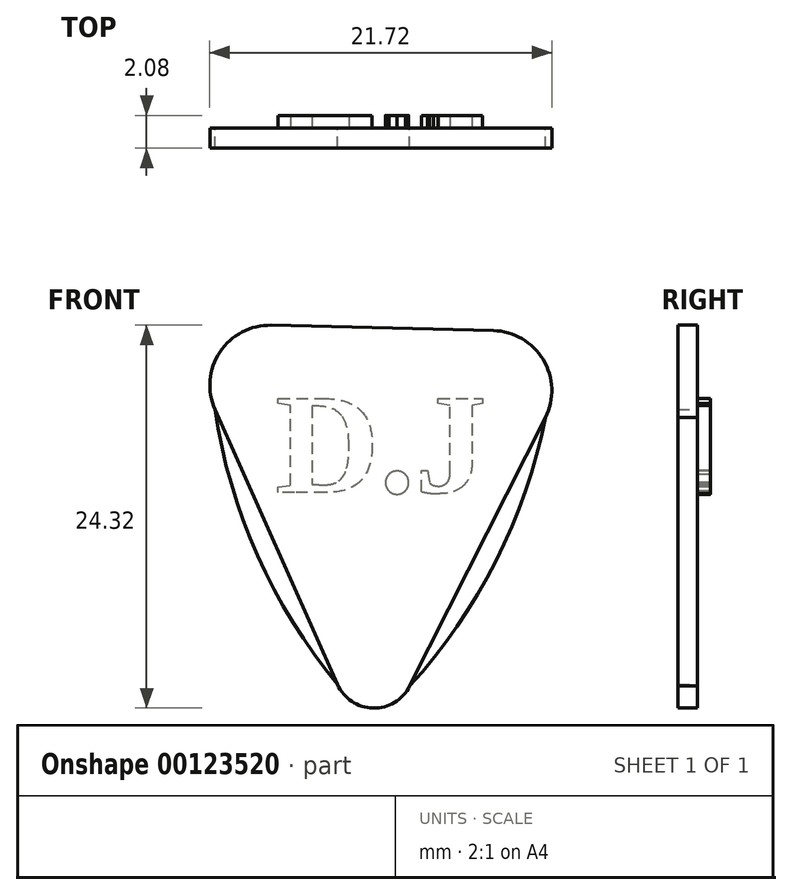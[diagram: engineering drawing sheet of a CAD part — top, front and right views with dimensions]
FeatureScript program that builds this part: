
annotation { "Feature Type Name" : "Feature", "Feature Type Description" : "" }
export const myFeature = defineFeature(function(context is Context, id is Id, definition is map)
    precondition{}
    {
        {
            var Q0;
            Q0=qCreatedBy(makeId("Front.planeOp"),FACE);
            var sketch = newSketch(context, id + "F0", { "sketchPlane" : qUnion([Q0])});
            skLineSegment(sketch, "E0", {"start": v(-9.96, 5.25) * mm, "end": v(-2.18, -12.2) * mm});
            skLineSegment(sketch, "E1", {"start": v(2.4, -12.31) * mm, "end": v(11.02, 4.74) * mm});
            skLineSegment(sketch, "E2", {"start": v(7.71, 10.27) * mm, "end": v(-6.39, 10.61) * mm});
            skPoint(sketch, "E3.visualSharp", {"position": v(13.74, 10.12) * mm});
            skArc(sketch, "E3.filletArc", {"start": v(11.02, 4.74) * mm, "mid": v(10.9, 8.42) * mm, "end": v(7.71, 10.27) * mm});
            skPoint(sketch, "E4.visualSharp", {"position": v(-12.41, 10.76) * mm});
            skArc(sketch, "E4.filletArc", {"start": v(-6.39, 10.61) * mm, "mid": v(-9.65, 8.91) * mm, "end": v(-9.96, 5.25) * mm});
            skPoint(sketch, "E5.visualSharp", {"position": v(0, -17.08) * mm});
            skArc(sketch, "E5.filletArc", {"start": v(-2.18, -12.2) * mm, "mid": v(0.08, -13.7) * mm, "end": v(2.4, -12.31) * mm});
            skArc(sketch, "E6", {"start": v(-9.96, 5.25) * mm, "mid": v(-7.26, -4) * mm, "end": v(-2.18, -12.2) * mm});
            skArc(sketch, "E7", {"start": v(2.4, -12.31) * mm, "mid": v(7.88, -4.37) * mm, "end": v(11.02, 4.74) * mm});
            skSolve(sketch);
        }
        {
            var Q0;
            Q0=makeQuery(id+"F0.imprint","IMPRINT",FACE,{"disambiguationData":[TD([[makeQuery(id+"F0.imprint","IMPRINT",EDGE,{"derivedFrom":sQuery(id+"F0.wireOp",EDGE,"E0")}),1.0]])]});
            extrude(context, id + "F1", {"entities" : qUnion([Q0]), "depth" : 1.26 * mm});
        }
        {
            var Q0;
            Q0=makeQuery(id+"F0.imprint","IMPRINT",FACE,{"disambiguationData":[TD([[makeQuery(id+"F0.imprint","IMPRINT",EDGE,{"derivedFrom":sQuery(id+"F0.wireOp",EDGE,"E0")}),-1.0]])]});
            var Q1;
            Q1=makeQuery(id+"F0.imprint","IMPRINT",FACE,{"disambiguationData":[TD([[makeQuery(id+"F0.imprint","IMPRINT",EDGE,{"derivedFrom":sQuery(id+"F0.wireOp",EDGE,"E1")}),-1.0]])]});
            extrude(context, id + "F2", {"entities" : qUnion([Q0, Q1]), "operationType" : NewBodyOperationType.ADD, "depth" : 1.27 * mm});
        }
        {
            var Q0;
            Q0=qCreatedBy(makeId("Front.planeOp"),FACE);
            var sketch = newSketch(context, id + "F3", { "sketchPlane" : qUnion([Q0])});
            skText(sketch, "E8", { "text": "D.J", "fontName": "Tinos-Bold.ttf"});
            const initialGuessF3  = {"E8": [-0.0061, 0, 1, 0, 0.00655]};
            skSetInitialGuess(sketch, initialGuessF3);
            skSolve(sketch);
        }
        {
            var Q0;
            Q0 = qSketchRegion(id + "F3", true);
            extrude(context, id + "F4", {"entities" : qUnion([Q0]), "operationType" : NewBodyOperationType.ADD, "oppositeDirection" : true, "depth" : 0.8 * mm});
        }
    });
